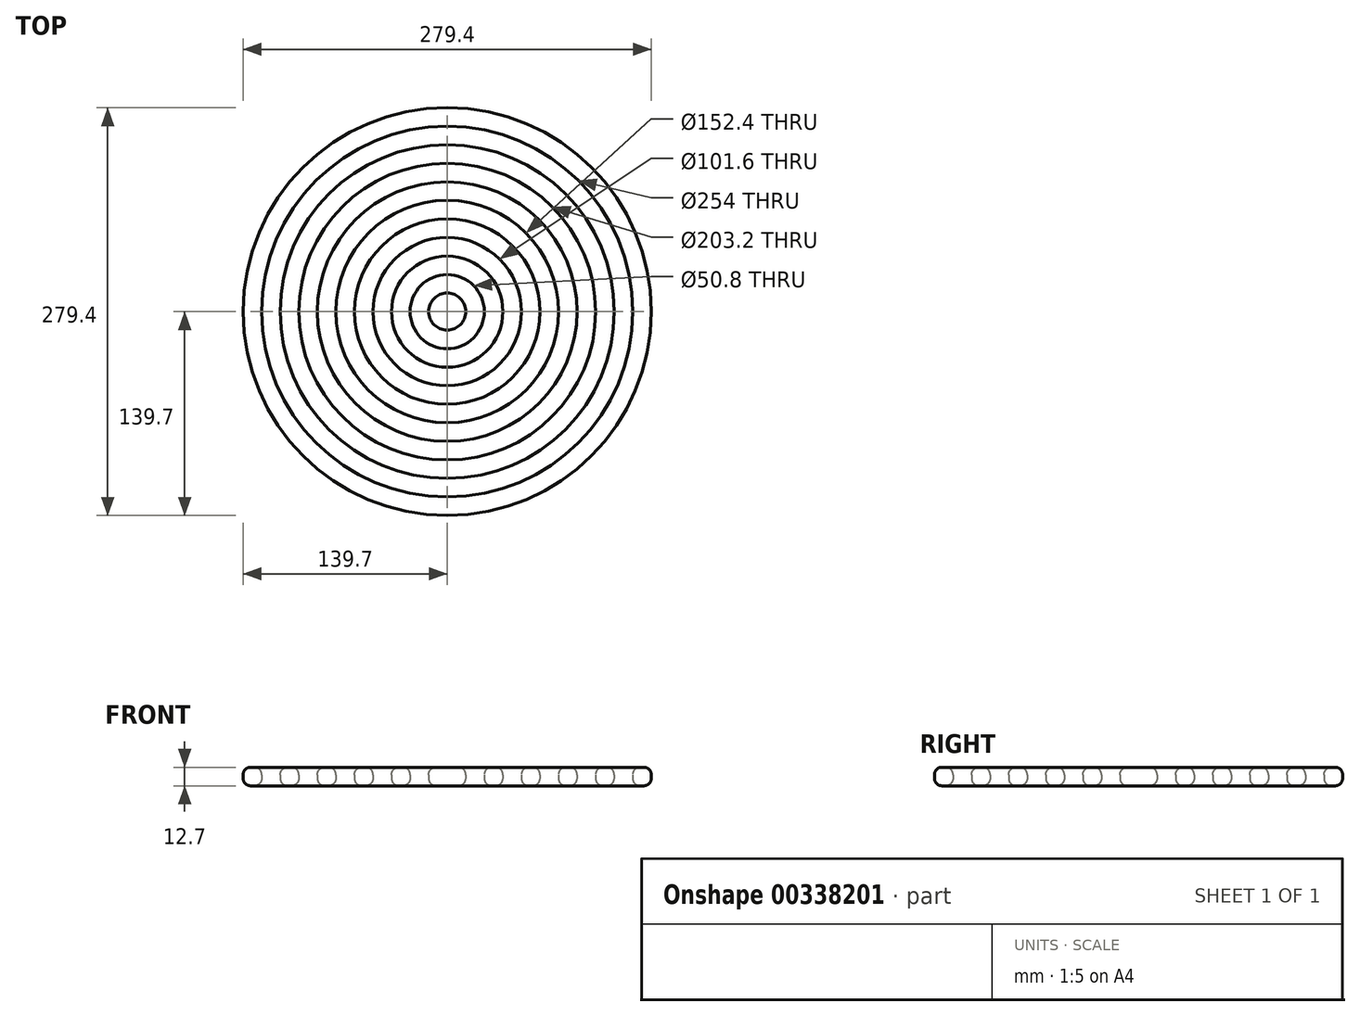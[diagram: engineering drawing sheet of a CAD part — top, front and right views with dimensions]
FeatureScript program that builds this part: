
annotation { "Feature Type Name" : "Feature", "Feature Type Description" : "" }
export const myFeature = defineFeature(function(context is Context, id is Id, definition is map)
    precondition{}
    {
        {
            var Q0;
            Q0=qCreatedBy(makeId("Top.planeOp"),FACE);
            var sketch = newSketch(context, id + "F0", { "sketchPlane" : qUnion([Q0])});
            skCircle(sketch, "E0", {"center": v(0, 0) * mm, "radius": 127 * mm});
            skLineSegment(sketch, "E1", {"start": v(25.4, 0) * mm, "end": v(25.4, 0) * mm});
            skLineSegment(sketch, "E2", {"start": v(38.1, 0) * mm, "end": v(50.8, 0) * mm});
            skLineSegment(sketch, "E3", {"start": v(12.7, 0) * mm, "end": v(12.7, 0) * mm});
            skLineSegment(sketch, "E4", {"start": v(25.4, 0) * mm, "end": v(38.1, 0) * mm});
            skLineSegment(sketch, "E5", {"start": v(24.92, -4.9) * mm, "end": v(24.92, -4.9) * mm});
            skCircle(sketch, "E6", {"center": v(0, 0) * mm, "radius": 50.8 * mm});
            skCircle(sketch, "E7", {"center": v(0, 0) * mm, "radius": 38.1 * mm});
            skCircle(sketch, "E8", {"center": v(0, 0) * mm, "radius": 25.4 * mm});
            skLineSegment(sketch, "E9", {"start": v(0, 0) * mm, "end": v(12.7, 0) * mm});
            skLineSegment(sketch, "E10", {"start": v(12.7, 0) * mm, "end": v(25.4, 0) * mm});
            skLineSegment(sketch, "E11", {"start": v(50.8, 0) * mm, "end": v(63.5, 0) * mm});
            skLineSegment(sketch, "E12", {"start": v(63.5, 0) * mm, "end": v(76.2, 0) * mm});
            skLineSegment(sketch, "E13", {"start": v(76.2, 0) * mm, "end": v(88.9, 0) * mm});
            skLineSegment(sketch, "E14", {"start": v(88.9, 0) * mm, "end": v(101.6, 0) * mm});
            skCircle(sketch, "E15", {"center": v(0, 0) * mm, "radius": 63.5 * mm});
            skCircle(sketch, "E16", {"center": v(0, 0) * mm, "radius": 76.2 * mm});
            skCircle(sketch, "E17", {"center": v(0, 0) * mm, "radius": 88.9 * mm});
            skCircle(sketch, "E18", {"center": v(0, 0) * mm, "radius": 101.6 * mm});
            skLineSegment(sketch, "E19", {"start": v(101.6, 0) * mm, "end": v(114.3, 0) * mm});
            skLineSegment(sketch, "E20", {"start": v(114.3, 0) * mm, "end": v(127, 0) * mm});
            skCircle(sketch, "E21", {"center": v(0, 0) * mm, "radius": 114.3 * mm});
            skCircle(sketch, "E22", {"center": v(0, 0) * mm, "radius": 139.7 * mm});
            skLineSegment(sketch, "E23", {"start": v(127, 0) * mm, "end": v(139.7, 0) * mm});
            skCircle(sketch, "E24", {"center": v(0, 0) * mm, "radius": 12.7 * mm});
            skLineSegment(sketch, "E25", {"start": v(4.99, -11.68) * mm, "end": v(107.87, -132.5) * mm, "construction": true});
            skLineSegment(sketch, "E26", {"start": v(10.42, -7.26) * mm, "end": v(113.37, -128.16) * mm, "construction": true});
            skSolve(sketch);
        }
        {
            var Q0;
            Q0 = qSketchRegion(id + "F0", true);
            var Q1;
            Q1=makeQuery(id+"F0.imprint","IMPRINT",FACE,{"disambiguationData":[TD([[makeQuery(id+"F0.imprint","IMPRINT",EDGE,{"derivedFrom":sQuery(id+"F0.wireOp",EDGE,"E18")}),-1.0]])]});
            var Q2;
            Q2=makeQuery(id+"F0.imprint","IMPRINT",FACE,{"disambiguationData":[TD([[makeQuery(id+"F0.imprint","IMPRINT",EDGE,{"derivedFrom":sQuery(id+"F0.wireOp",EDGE,"E16")}),-1.0]])]});
            var Q3;
            Q3=makeQuery(id+"F0.imprint","IMPRINT",FACE,{"disambiguationData":[TD([[makeQuery(id+"F0.imprint","IMPRINT",EDGE,{"derivedFrom":sQuery(id+"F0.wireOp",EDGE,"E6")}),-1.0]])]});
            var Q4;
            Q4=makeQuery(id+"F0.imprint","IMPRINT",FACE,{"disambiguationData":[TD([[makeQuery(id+"F0.imprint","IMPRINT",EDGE,{"derivedFrom":sQuery(id+"F0.wireOp",EDGE,"E7")}),1.0]])]});
            var Q5;
            Q5=makeQuery(id+"F0.imprint","IMPRINT",FACE,{"disambiguationData":[TD([[makeQuery(id+"F0.imprint","IMPRINT",EDGE,{"derivedFrom":sQuery(id+"F0.wireOp",EDGE,"E24")}),1.0]])]});
            var Q6;
            {var subQ0=sQuery(id+"F0.wireOp",EDGE,"b48a7bee-8bd0-474f-ad38-98021d52fab4");Q6=makeQuery(id+"F0.imprint","IMPRINT",FACE,{"disambiguationData":[TD([[makeQuery(id+"F0.imprint","IMPRINT",EDGE,{"derivedFrom":subQ0}),-1.0]])]});}
            extrude(context, id + "F1", {"entities" : qUnion([Q0, Q1, Q2, Q3, Q4, Q5, Q6]), "depth" : 12.7 * mm});
        }
        {
            var Q0;
            Q0=makeQuery(id+"F1.opExtrude","CAP_FACE",FACE,{"disambiguationData":[OSD([sQuery(id+"F0.wireOp",EDGE,"E24")])],"isStart":true});
            var Q1;
            Q1=makeQuery(id+"F1.opExtrude","SWEPT_FACE",FACE,{"disambiguationData":[OSD([sQuery(id+"F0.wireOp",EDGE,"E24")])]});
            var Q2;
            Q2=makeQuery(id+"F1.opExtrude","CAP_FACE",FACE,{"disambiguationData":[OSD([sQuery(id+"F0.wireOp",EDGE,"E24")])],"isStart":false});
            fillet(context, id + "F2", {"entities" : qUnion([Q0, Q1, Q2]), "radius" : 5.08 * mm, "tangentPropagation" : true, "allowEdgeOverflow" : false});
        }
        {
            var Q0;
            Q0=makeQuery(id+"F1.opExtrude","SWEPT_FACE",FACE,{"disambiguationData":[OSD([sQuery(id+"F0.wireOp",EDGE,"E7")])]});
            var Q1;
            Q1=makeQuery(id+"F1.opExtrude","CAP_FACE",FACE,{"disambiguationData":[OSD([sQuery(id+"F0.wireOp",EDGE,"E7"),sQuery(id+"F0.wireOp",EDGE,"E8")])],"isStart":false});
            var Q2;
            Q2=makeQuery(id+"F1.opExtrude","CAP_FACE",FACE,{"disambiguationData":[OSD([sQuery(id+"F0.wireOp",EDGE,"E7"),sQuery(id+"F0.wireOp",EDGE,"E8")])],"isStart":true});
            var Q3;
            Q3=makeQuery(id+"F1.opExtrude","SWEPT_FACE",FACE,{"disambiguationData":[OSD([sQuery(id+"F0.wireOp",EDGE,"E8")])]});
            fillet(context, id + "F3", {"entities" : qUnion([Q0, Q1, Q2, Q3]), "radius" : 5.08 * mm, "tangentPropagation" : true, "allowEdgeOverflow" : false});
        }
        {
            var Q0;
            Q0=makeQuery(id+"F1.opExtrude","CAP_FACE",FACE,{"disambiguationData":[OSD([sQuery(id+"F0.wireOp",EDGE,"E6"),sQuery(id+"F0.wireOp",EDGE,"E15")])],"isStart":false});
            var Q1;
            Q1=makeQuery(id+"F1.opExtrude","SWEPT_FACE",FACE,{"disambiguationData":[OSD([sQuery(id+"F0.wireOp",EDGE,"E6")])]});
            var Q2;
            Q2=makeQuery(id+"F1.opExtrude","CAP_FACE",FACE,{"disambiguationData":[OSD([sQuery(id+"F0.wireOp",EDGE,"E6"),sQuery(id+"F0.wireOp",EDGE,"E15")])],"isStart":true});
            var Q3;
            Q3=makeQuery(id+"F1.opExtrude","SWEPT_FACE",FACE,{"disambiguationData":[OSD([sQuery(id+"F0.wireOp",EDGE,"E15")])]});
            fillet(context, id + "F4", {"entities" : qUnion([Q0, Q1, Q2, Q3]), "radius" : 5.08 * mm, "tangentPropagation" : true, "allowEdgeOverflow" : false});
        }
        {
            var Q0;
            Q0=makeQuery(id+"F1.opExtrude","SWEPT_FACE",FACE,{"disambiguationData":[OSD([sQuery(id+"F0.wireOp",EDGE,"E16")])]});
            var Q1;
            Q1=makeQuery(id+"F1.opExtrude","CAP_FACE",FACE,{"disambiguationData":[OSD([sQuery(id+"F0.wireOp",EDGE,"E16"),sQuery(id+"F0.wireOp",EDGE,"E17")])],"isStart":false});
            var Q2;
            Q2=makeQuery(id+"F1.opExtrude","CAP_FACE",FACE,{"disambiguationData":[OSD([sQuery(id+"F0.wireOp",EDGE,"E16"),sQuery(id+"F0.wireOp",EDGE,"E17")])],"isStart":true});
            var Q3;
            Q3=makeQuery(id+"F1.opExtrude","SWEPT_FACE",FACE,{"disambiguationData":[OSD([sQuery(id+"F0.wireOp",EDGE,"E17")])]});
            fillet(context, id + "F5", {"entities" : qUnion([Q0, Q1, Q2, Q3]), "radius" : 5.08 * mm, "tangentPropagation" : true, "allowEdgeOverflow" : false});
        }
        {
            var Q0;
            Q0=makeQuery(id+"F1.opExtrude","CAP_FACE",FACE,{"disambiguationData":[OSD([sQuery(id+"F0.wireOp",EDGE,"E0"),sQuery(id+"F0.wireOp",EDGE,"E22")])],"isStart":false});
            var Q1;
            Q1=makeQuery(id+"F1.opExtrude","SWEPT_FACE",FACE,{"disambiguationData":[OSD([sQuery(id+"F0.wireOp",EDGE,"E18")])]});
            var Q2;
            Q2=makeQuery(id+"F1.opExtrude","CAP_FACE",FACE,{"disambiguationData":[OSD([sQuery(id+"F0.wireOp",EDGE,"E18"),sQuery(id+"F0.wireOp",EDGE,"E21")])],"isStart":true});
            var Q3;
            Q3=makeQuery(id+"F1.opExtrude","CAP_FACE",FACE,{"disambiguationData":[OSD([sQuery(id+"F0.wireOp",EDGE,"E0"),sQuery(id+"F0.wireOp",EDGE,"E22")])],"isStart":true});
            var Q4;
            Q4=makeQuery(id+"F1.opExtrude","SWEPT_FACE",FACE,{"disambiguationData":[OSD([sQuery(id+"F0.wireOp",EDGE,"E0")])]});
            var Q5;
            Q5=makeQuery(id+"F1.opExtrude","SWEPT_FACE",FACE,{"disambiguationData":[OSD([sQuery(id+"F0.wireOp",EDGE,"E22")])]});
            var Q6;
            Q6=makeQuery(id+"F1.opExtrude","CAP_FACE",FACE,{"disambiguationData":[OSD([sQuery(id+"F0.wireOp",EDGE,"E18"),sQuery(id+"F0.wireOp",EDGE,"E21")])],"isStart":false});
            var Q7;
            Q7=makeQuery(id+"F1.opExtrude","SWEPT_FACE",FACE,{"disambiguationData":[OSD([sQuery(id+"F0.wireOp",EDGE,"E21")])]});
            fillet(context, id + "F6", {"entities" : qUnion([Q0, Q1, Q2, Q3, Q4, Q5, Q6, Q7]), "radius" : 5.08 * mm, "tangentPropagation" : true, "allowEdgeOverflow" : false});
        }
    });
